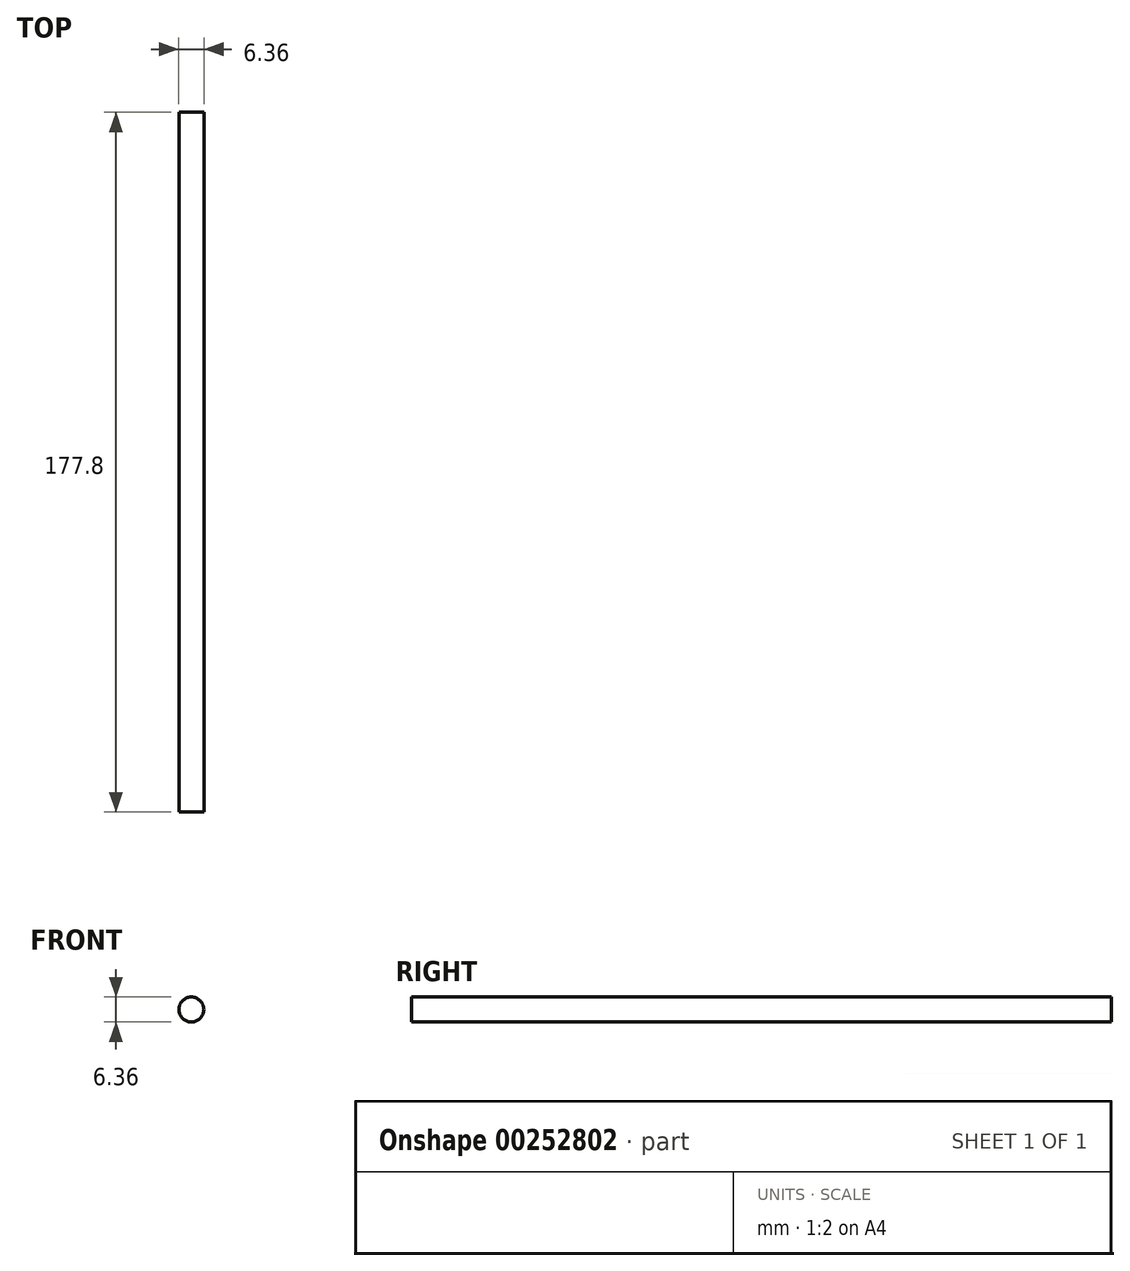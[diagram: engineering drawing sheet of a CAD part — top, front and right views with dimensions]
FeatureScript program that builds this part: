
annotation { "Feature Type Name" : "Feature", "Feature Type Description" : "" }
export const myFeature = defineFeature(function(context is Context, id is Id, definition is map)
    precondition{}
    {
        {
            var Q0;
            Q0=qCreatedBy(makeId("Front.planeOp"),FACE);
            var sketch = newSketch(context, id + "F0", { "sketchPlane" : qUnion([Q0])});
            skCircle(sketch, "E0", {"center": v(0, 0) * mm, "radius": 3.17 * mm});
            skSolve(sketch);
        }
        {
            var Q0;
            Q0 = qSketchRegion(id + "F0", true);
            extrude(context, id + "F1", {"entities" : qUnion([Q0]), "depth" : 177.8 * mm});
        }
    });
